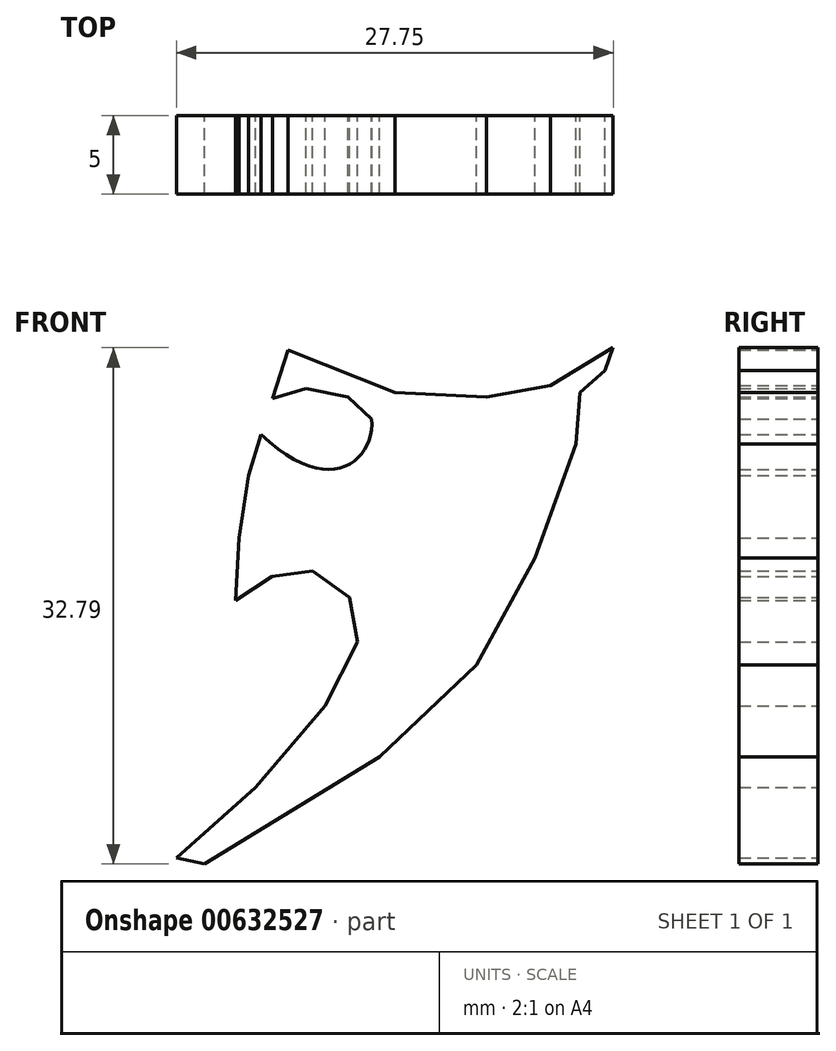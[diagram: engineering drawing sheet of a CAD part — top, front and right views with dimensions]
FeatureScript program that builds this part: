
annotation { "Feature Type Name" : "Feature", "Feature Type Description" : "" }
export const myFeature = defineFeature(function(context is Context, id is Id, definition is map)
    precondition{}
    {
        {
            var Q0;
            Q0=qCreatedBy(makeId("Front.planeOp"),FACE);
            var sketch = newSketch(context, id + "F0", { "sketchPlane" : qUnion([Q0])});
            skLineSegment(sketch, "E0", {"start": v(7.3, -0.15) * mm, "end": v(6.31, -3.23) * mm});
            skLineSegment(sketch, "E1", {"start": v(6.31, -3.23) * mm, "end": v(8.43, -2.6) * mm});
            skLineSegment(sketch, "E2", {"start": v(8.43, -2.6) * mm, "end": v(11.1, -3.14) * mm});
            skLineSegment(sketch, "E3", {"start": v(11.1, -3.14) * mm, "end": v(12.6, -4.51) * mm});
            skFitSpline(sketch, "E4", {"points": [v(12.6, -4.51) * mm, v(5.57, -5.5) * mm], "startDerivative": vector(0.6, -8.28) * mm, "endDerivative": vector(-12.89, 12.32) * mm});
            skLineSegment(sketch, "E5", {"start": v(5.57, -5.5) * mm, "end": v(4.79, -8.11) * mm});
            skLineSegment(sketch, "E6", {"start": v(4.79, -8.11) * mm, "end": v(4.18, -12.08) * mm});
            skLineSegment(sketch, "E7", {"start": v(4.18, -12.08) * mm, "end": v(3.95, -16.04) * mm});
            skLineSegment(sketch, "E8", {"start": v(3.95, -16.04) * mm, "end": v(6.28, -14.52) * mm});
            skLineSegment(sketch, "E9", {"start": v(6.28, -14.52) * mm, "end": v(8.84, -14.16) * mm});
            skLineSegment(sketch, "E10", {"start": v(8.84, -14.16) * mm, "end": v(11.19, -15.85) * mm});
            skLineSegment(sketch, "E11", {"start": v(11.19, -15.85) * mm, "end": v(11.7, -18.69) * mm});
            skLineSegment(sketch, "E12", {"start": v(11.7, -18.69) * mm, "end": v(9.64, -22.75) * mm});
            skLineSegment(sketch, "E13", {"start": v(9.64, -22.75) * mm, "end": v(5.23, -27.91) * mm});
            skLineSegment(sketch, "E14", {"start": v(5.23, -27.91) * mm, "end": v(0.2, -32.4) * mm});
            skLineSegment(sketch, "E15", {"start": v(0.2, -32.4) * mm, "end": v(2, -32.8) * mm});
            skLineSegment(sketch, "E16", {"start": v(2, -32.8) * mm, "end": v(13.1, -26) * mm});
            skLineSegment(sketch, "E17", {"start": v(13.1, -26) * mm, "end": v(19.26, -20.15) * mm});
            skLineSegment(sketch, "E18", {"start": v(19.26, -20.15) * mm, "end": v(22.98, -13.37) * mm});
            skLineSegment(sketch, "E19", {"start": v(22.98, -13.37) * mm, "end": v(25.57, -6.1) * mm});
            skLineSegment(sketch, "E20", {"start": v(25.57, -6.1) * mm, "end": v(25.84, -2.86) * mm});
            skLineSegment(sketch, "E21", {"start": v(25.84, -2.86) * mm, "end": v(27.44, -1.43) * mm});
            skLineSegment(sketch, "E22", {"start": v(27.44, -1.43) * mm, "end": v(27.95, 0) * mm});
            skLineSegment(sketch, "E23", {"start": v(27.95, 0) * mm, "end": v(23.96, -2.4) * mm});
            skLineSegment(sketch, "E24", {"start": v(23.96, -2.4) * mm, "end": v(19.92, -3.12) * mm});
            skLineSegment(sketch, "E25", {"start": v(19.92, -3.12) * mm, "end": v(14.08, -2.86) * mm});
            skLineSegment(sketch, "E26", {"start": v(14.08, -2.86) * mm, "end": v(7.3, -0.15) * mm});
            skSolve(sketch);
        }
        {
            var Q0;
            Q0=makeQuery(id+"F0.imprint","IMPRINT",FACE,{"disambiguationData":[TD([[makeQuery(id+"F0.imprint","IMPRINT",EDGE,{"derivedFrom":sQuery(id+"F0.wireOp",EDGE,"E0")}),1.0]])]});
            extrude(context, id + "F1", {"entities" : qUnion([Q0]), "depth" : 5 * mm, "offsetDistance" : 25 * mm});
        }
    });
